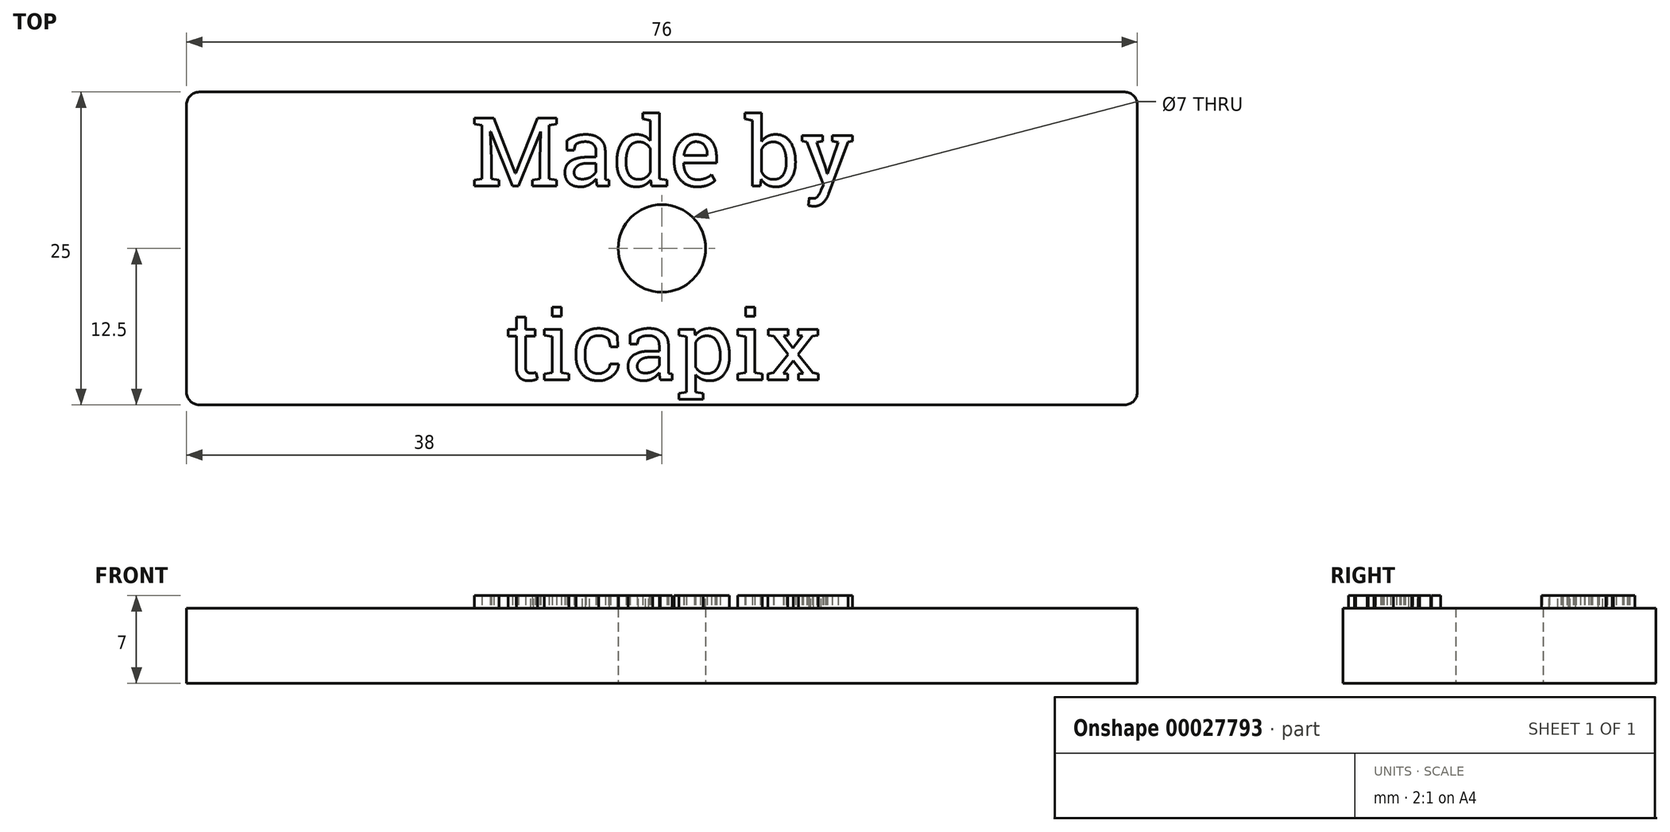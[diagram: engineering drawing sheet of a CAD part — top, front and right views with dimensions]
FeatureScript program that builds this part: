
annotation { "Feature Type Name" : "Feature", "Feature Type Description" : "" }
export const myFeature = defineFeature(function(context is Context, id is Id, definition is map)
    precondition{}
    {
        {
            var Q0;
            Q0=qCreatedBy(makeId("Top.planeOp"),FACE);
            var sketch = newSketch(context, id + "F0", { "sketchPlane" : qUnion([Q0])});
            skLineSegment(sketch, "E0.bottom", {"start": v(-38, 12.5) * mm, "end": v(38, 12.5) * mm});
            skLineSegment(sketch, "E0.top", {"start": v(-38, -12.5) * mm, "end": v(38, -12.5) * mm});
            skLineSegment(sketch, "E0.left", {"start": v(-38, 12.5) * mm, "end": v(-38, -12.5) * mm});
            skLineSegment(sketch, "E0.right", {"start": v(38, 12.5) * mm, "end": v(38, -12.5) * mm});
            skLineSegment(sketch, "E1", {"start": v(-38, -12.5) * mm, "end": v(38, 12.5) * mm, "construction": true});
            skCircle(sketch, "E2", {"center": v(0, 0) * mm, "radius": 3.5 * mm});
            skLineSegment(sketch, "E3", {"start": v(-30, 12.5) * mm, "end": v(-30, -12.5) * mm, "construction": true});
            skLineSegment(sketch, "E4.MirrorCS", {"start": v(30, 12.5) * mm, "end": v(30, -12.5) * mm, "construction": true});
            skSolve(sketch);
        }
        {
            var Q0;
            Q0 = qSketchRegion(id + "F0", true);
            extrude(context, id + "F1", {"entities" : qUnion([Q0]), "depth" : 6 * mm, "symmetric" : true});
        }
        {
            var Q0;
            Q0=makeQuery(id+"F1.opExtrude","SWEPT_EDGE",EDGE,{"disambiguationData":[OSD([sQuery(id+"F0.wireOp",EDGE,"E0.bottom"),sQuery(id+"F0.wireOp",EDGE,"E0.right")])]});
            var Q1;
            Q1=makeQuery(id+"F1.opExtrude","SWEPT_EDGE",EDGE,{"disambiguationData":[OSD([sQuery(id+"F0.wireOp",EDGE,"E0.top"),sQuery(id+"F0.wireOp",EDGE,"E0.right")])]});
            var Q2;
            Q2=makeQuery(id+"F1.opExtrude","SWEPT_EDGE",EDGE,{"disambiguationData":[OSD([sQuery(id+"F0.wireOp",EDGE,"E0.top"),sQuery(id+"F0.wireOp",EDGE,"E0.left")])]});
            var Q3;
            Q3=makeQuery(id+"F1.opExtrude","SWEPT_EDGE",EDGE,{"disambiguationData":[OSD([sQuery(id+"F0.wireOp",EDGE,"E0.bottom"),sQuery(id+"F0.wireOp",EDGE,"E0.left")])]});
            fillet(context, id + "F2", {"entities" : qUnion([Q0, Q1, Q2, Q3]), "radius" : 1 * mm, "tangentPropagation" : true, "allowEdgeOverflow" : false});
        }
        {
            var Q0;
            Q0=makeQuery(id+"F1.opExtrude","CAP_FACE",FACE,{"disambiguationData":[OSD([sQuery(id+"F0.wireOp",EDGE,"E0.bottom"),sQuery(id+"F0.wireOp",EDGE,"E0.top"),sQuery(id+"F0.wireOp",EDGE,"E0.left"),sQuery(id+"F0.wireOp",EDGE,"E0.right"),sQuery(id+"F0.wireOp",EDGE,"E2")])],"isStart":false});
            var sketch = newSketch(context, id + "F3", { "sketchPlane" : qUnion([Q0])});
            skText(sketch, "E5", { "text": "ticapix", "fontName": "RobotoSlab-Regular.ttf"});
            skText(sketch, "E6", { "text": "Made by", "fontName": "RobotoSlab-Regular.ttf"});
            skPoint(sketch, "E7", {"position": v(0, 10.5) * mm});
            skPoint(sketch, "E8", {"position": v(0, -5) * mm});
            const initialGuessF3  = {"E5": [-0.01252, -0.0105, 1, 0, 0.0055], "E6": [-0.01525, 0.005, 1, 0, 0.0055]};
            skSetInitialGuess(sketch, initialGuessF3);
            skSolve(sketch);
        }
        {
            var Q0;
            Q0 = qSketchRegion(id + "F3", true);
            extrude(context, id + "F4", {"entities" : qUnion([Q0]), "operationType" : NewBodyOperationType.ADD, "depth" : 1 * mm});
        }
    });
